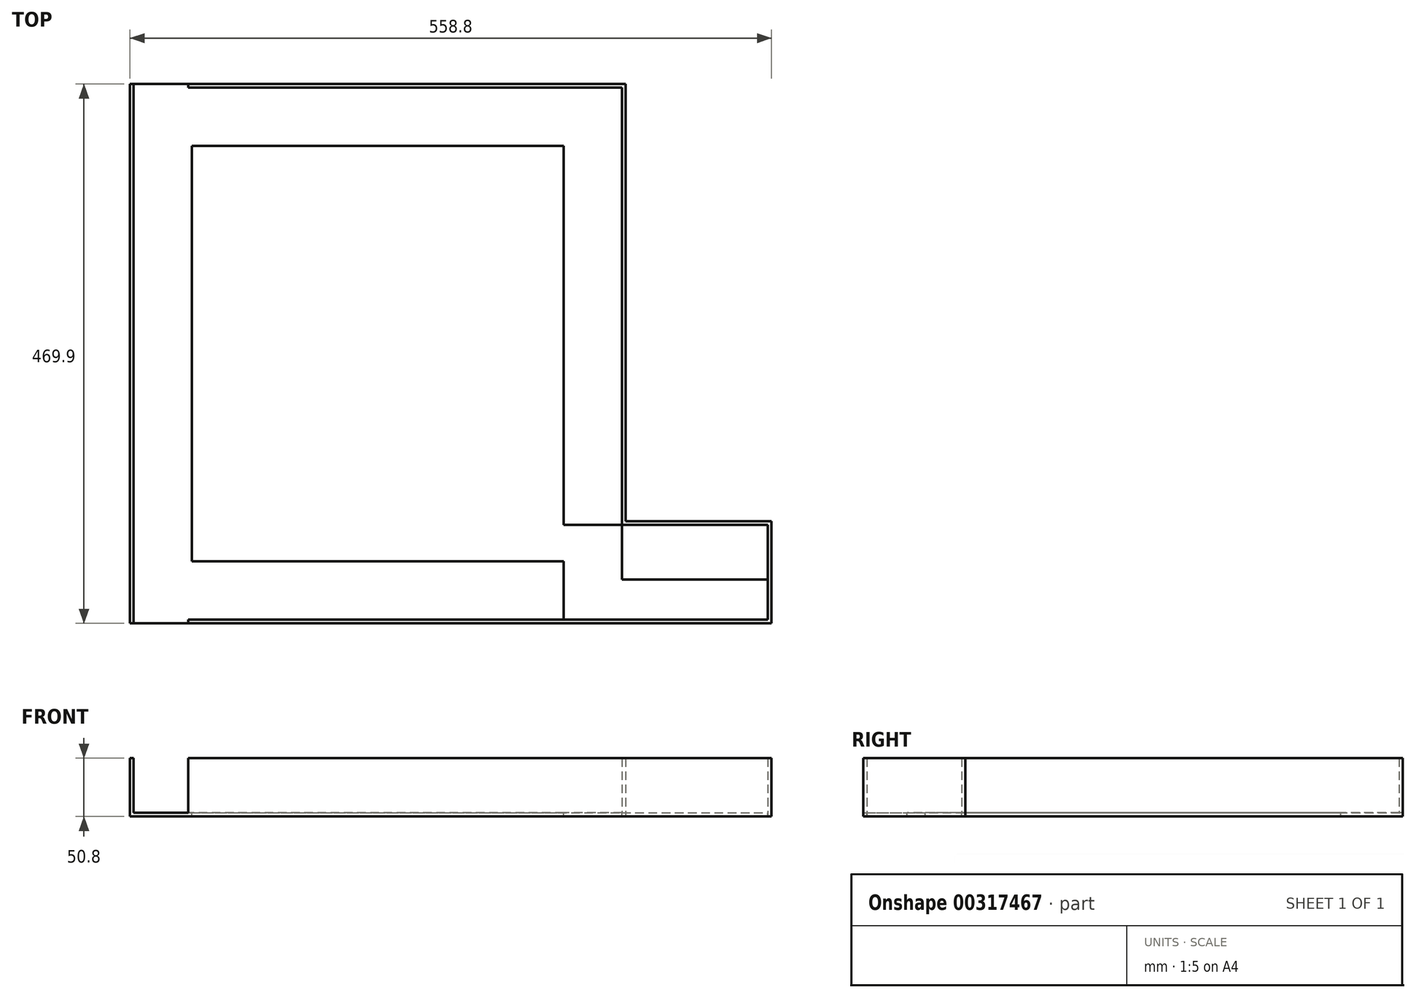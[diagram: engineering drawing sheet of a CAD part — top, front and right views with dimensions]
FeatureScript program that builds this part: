
annotation { "Feature Type Name" : "Feature", "Feature Type Description" : "" }
export const myFeature = defineFeature(function(context is Context, id is Id, definition is map)
    precondition{}
    {
        {
            var Q0;
            Q0=qCreatedBy(makeId("Top.planeOp"),FACE);
            var sketch = newSketch(context, id + "F0", { "sketchPlane" : qUnion([Q0])});
            skLineSegment(sketch, "E0", {"start": v(-298.12, 0) * mm, "end": v(-298.12, 269.38) * mm});
            skLineSegment(sketch, "E1", {"start": v(-298.12, 269.38) * mm, "end": v(133.68, 269.38) * mm});
            skLineSegment(sketch, "E2", {"start": v(133.68, 269.38) * mm, "end": v(133.68, -111.62) * mm});
            skLineSegment(sketch, "E3", {"start": v(133.68, -111.62) * mm, "end": v(260.68, -111.62) * mm});
            skLineSegment(sketch, "E4", {"start": v(260.68, -111.62) * mm, "end": v(260.68, -200.52) * mm});
            skLineSegment(sketch, "E5", {"start": v(260.68, -200.52) * mm, "end": v(-298.12, -200.52) * mm});
            skLineSegment(sketch, "E6", {"start": v(-298.12, -200.52) * mm, "end": v(-298.12, 0) * mm});
            skSolve(sketch);
        }
        {
            var Q0;
            Q0 = qSketchRegion(id + "F0", true);
            extrude(context, id + "F1", {"entities" : qUnion([Q0]), "depth" : 50.8 * mm});
        }
        {
            var Q0;
            Q0=makeQuery(id+"F1.opExtrude","CAP_FACE",FACE,{"disambiguationData":[OSD([sQuery(id+"F0.wireOp",EDGE,"E0"),sQuery(id+"F0.wireOp",EDGE,"E1"),sQuery(id+"F0.wireOp",EDGE,"E2"),sQuery(id+"F0.wireOp",EDGE,"E3"),sQuery(id+"F0.wireOp",EDGE,"E4"),sQuery(id+"F0.wireOp",EDGE,"E5"),sQuery(id+"F0.wireOp",EDGE,"E6")])],"isStart":false});
            shell(context, id + "F2", {"entities" : qUnion([Q0]), "thickness" : 3.17 * mm});
        }
        {
            var Q0;
            Q0=makeQuery(id+"F2.opShell","OFFSET_FACE",FACE,{"disambiguationData":[OSD([sQuery(id+"F0.wireOp",EDGE,"E0"),sQuery(id+"F0.wireOp",EDGE,"E1"),sQuery(id+"F0.wireOp",EDGE,"E2"),sQuery(id+"F0.wireOp",EDGE,"E3"),sQuery(id+"F0.wireOp",EDGE,"E4"),sQuery(id+"F0.wireOp",EDGE,"E5"),sQuery(id+"F0.wireOp",EDGE,"E6")])]});
            var sketch = newSketch(context, id + "F3", { "sketchPlane" : qUnion([Q0])});
            skLineSegment(sketch, "E7.0", {"start": v(-244.15, 215.4) * mm, "end": v(-244.15, -146.54) * mm});
            skLineSegment(sketch, "E7.1", {"start": v(79.7, 215.4) * mm, "end": v(-244.15, 215.4) * mm});
            skLineSegment(sketch, "E7.2", {"start": v(79.7, -146.54) * mm, "end": v(79.7, 215.4) * mm});
            skLineSegment(sketch, "E7.3", {"start": v(-244.15, -146.54) * mm, "end": v(79.7, -146.54) * mm});
            skSolve(sketch);
        }
        {
            var Q0;
            Q0 = qSketchRegion(id + "F3", true);
            extrude(context, id + "F4", {"entities" : qUnion([Q0]), "operationType" : NewBodyOperationType.REMOVE, "oppositeDirection" : true, "depth" : 25.4 * mm});
        }
        {
            var Q0;
            Q0=makeQuery(id+"F2.opShell","OFFSET_FACE",FACE,{"disambiguationData":[OSD([sQuery(id+"F0.wireOp",EDGE,"E1")])]});
            var sketch = newSketch(context, id + "F5", { "sketchPlane" : qUnion([Q0])});
            skLineSegment(sketch, "E8", {"start": v(-294.95, 3.18) * mm, "end": v(-247.32, 3.17) * mm});
            skLineSegment(sketch, "E9", {"start": v(-247.32, 3.17) * mm, "end": v(-247.32, 50.8) * mm});
            skLineSegment(sketch, "E10", {"start": v(-247.32, 50.8) * mm, "end": v(-294.95, 50.8) * mm});
            skLineSegment(sketch, "E11", {"start": v(-294.95, 50.8) * mm, "end": v(-294.95, 3.18) * mm});
            skSolve(sketch);
        }
        {
            var Q0;
            Q0=makeQuery(id+"F5.imprint","IMPRINT",FACE,{"disambiguationData":[TD([[makeQuery(id+"F5.imprint","IMPRINT",EDGE,{"derivedFrom":sQuery(id+"F5.wireOp",EDGE,"E8")}),1.0]])]});
            extrude(context, id + "F6", {"entities" : qUnion([Q0]), "operationType" : NewBodyOperationType.REMOVE, "endBound" : BoundingType.SYMMETRIC, "oppositeDirection" : true, "depth" : 508 * mm});
        }
        {
            var Q0;
            Q0=makeQuery(id+"F2.opShell","OFFSET_FACE",FACE,{"disambiguationData":[OSD([sQuery(id+"F0.wireOp",EDGE,"E5")])]});
            var sketch = newSketch(context, id + "F7", { "sketchPlane" : qUnion([Q0])});
            skLineSegment(sketch, "E12", {"start": v(294.95, 3.18) * mm, "end": v(294.95, 50.8) * mm});
            skLineSegment(sketch, "E13", {"start": v(294.95, 50.8) * mm, "end": v(247.32, 50.8) * mm});
            skLineSegment(sketch, "E14", {"start": v(247.32, 50.8) * mm, "end": v(247.32, 3.17) * mm});
            skLineSegment(sketch, "E15", {"start": v(247.32, 3.17) * mm, "end": v(294.95, 3.18) * mm});
            skSolve(sketch);
        }
        {
            var Q0;
            Q0 = qSketchRegion(id + "F7", true);
            extrude(context, id + "F8", {"entities" : qUnion([Q0]), "operationType" : NewBodyOperationType.REMOVE, "oppositeDirection" : true, "depth" : 25.4 * mm});
        }
        {
            var Q0;
            Q0=makeQuery(id+"F8.boolean.opBoolean","MERGE",FACE,{"derivedFrom":[makeQuery(id+"F6.boolean.opBoolean","MERGE",FACE,{"derivedFrom":[makeQuery(id+"F2.opShell","OFFSET_FACE",FACE,{"disambiguationData":[OSD([sQuery(id+"F0.wireOp",EDGE,"E0"),sQuery(id+"F0.wireOp",EDGE,"E1"),sQuery(id+"F0.wireOp",EDGE,"E2"),sQuery(id+"F0.wireOp",EDGE,"E3"),sQuery(id+"F0.wireOp",EDGE,"E4"),sQuery(id+"F0.wireOp",EDGE,"E5"),sQuery(id+"F0.wireOp",EDGE,"E6")])]}),makeQuery(id+"F6.opExtrude","SWEPT_FACE",FACE,{"disambiguationData":[OSD([sQuery(id+"F5.wireOp",EDGE,"E8")])]})]}),makeQuery(id+"F8.opExtrude","SWEPT_FACE",FACE,{"disambiguationData":[OSD([sQuery(id+"F7.wireOp",EDGE,"E15")])]})]});
            var sketch = newSketch(context, id + "F9", { "sketchPlane" : qUnion([Q0])});
            skLineSegment(sketch, "E16", {"start": v(130.5, -114.8) * mm, "end": v(79.7, -114.8) * mm});
            skLineSegment(sketch, "E17", {"start": v(79.7, -114.8) * mm, "end": v(79.7, -197.34) * mm});
            skLineSegment(sketch, "E18", {"start": v(130.5, -114.8) * mm, "end": v(130.5, -162.42) * mm});
            skLineSegment(sketch, "E19", {"start": v(130.5, -162.42) * mm, "end": v(257.5, -162.42) * mm});
            skLineSegment(sketch, "E20", {"start": v(257.5, -162.42) * mm, "end": v(257.5, -197.34) * mm});
            skLineSegment(sketch, "E21", {"start": v(257.5, -197.34) * mm, "end": v(79.7, -197.34) * mm});
            skSolve(sketch);
        }
        {
            var Q0;
            Q0 = qSketchRegion(id + "F9", true);
            extrude(context, id + "F10", {"entities" : qUnion([Q0]), "operationType" : NewBodyOperationType.REMOVE, "oppositeDirection" : true, "depth" : 25.4 * mm});
        }
    });
